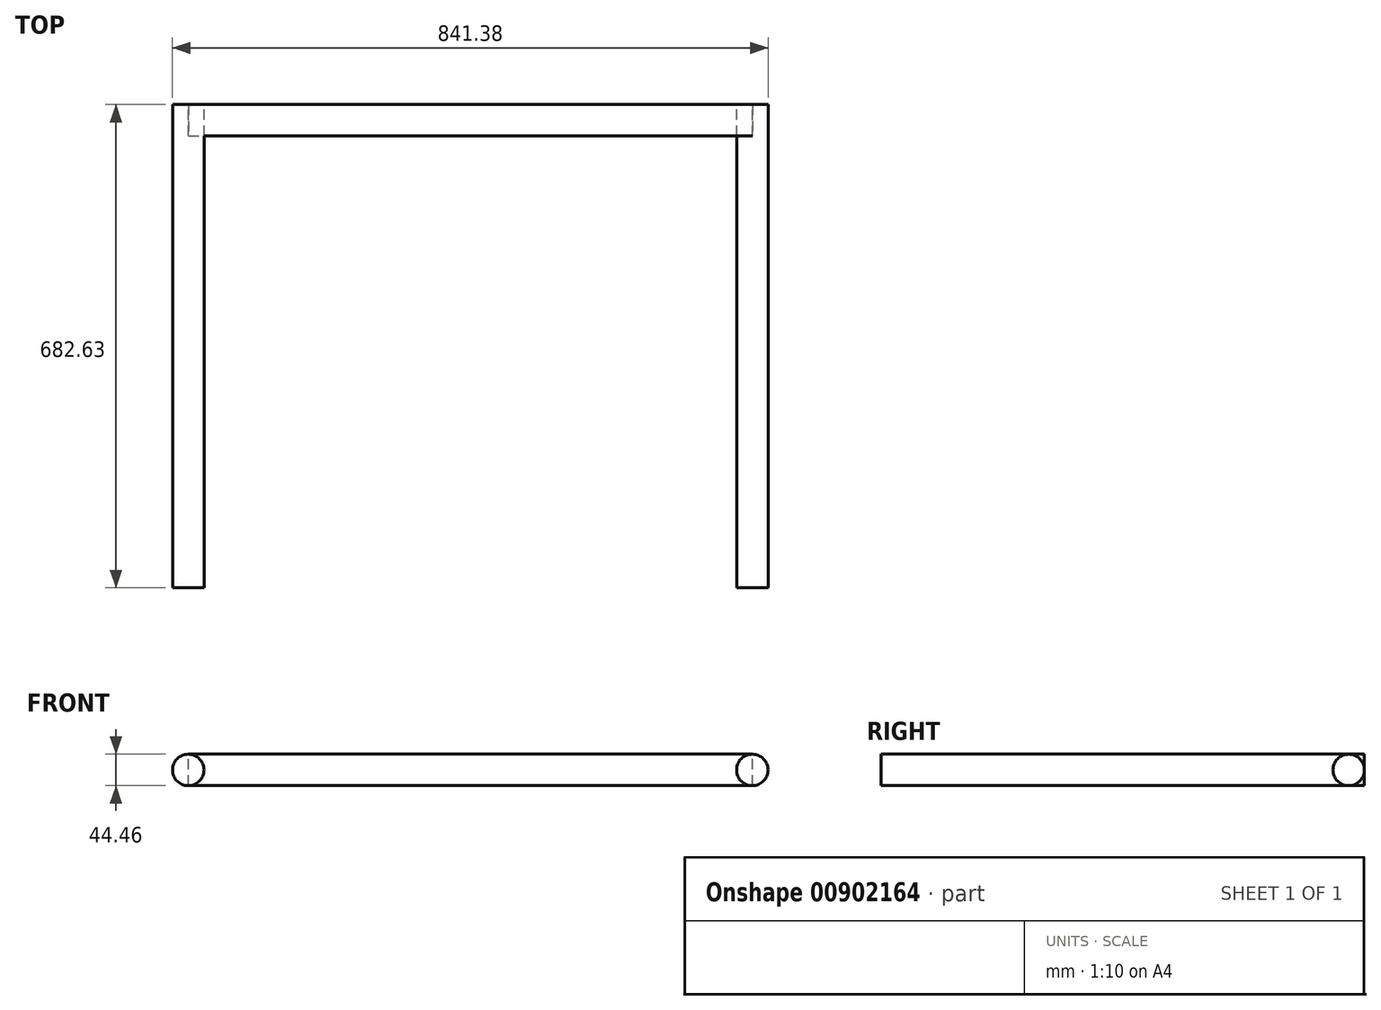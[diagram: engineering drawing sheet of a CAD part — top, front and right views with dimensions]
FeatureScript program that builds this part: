
annotation { "Feature Type Name" : "Feature", "Feature Type Description" : "" }
export const myFeature = defineFeature(function(context is Context, id is Id, definition is map)
    precondition{}
    {
        {
            var Q0;
            Q0=qCreatedBy(makeId("Front.planeOp"),FACE);
            var sketch = newSketch(context, id + "F0", { "sketchPlane" : qUnion([Q0])});
            skLineSegment(sketch, "E0", {"start": v(0, 0) * mm, "end": v(0, -387.35) * mm, "construction": true});
            skLineSegment(sketch, "E1", {"start": v(0, -387.35) * mm, "end": v(-398.46, -387.35) * mm, "construction": true});
            skLineSegment(sketch, "E2", {"start": v(0, -387.35) * mm, "end": v(398.46, -387.35) * mm, "construction": true});
            skSolve(sketch);
        }
        {
            var Q0;
            Q0=qCreatedBy(makeId("Front.planeOp"),FACE);
            var sketch = newSketch(context, id + "F1", { "sketchPlane" : qUnion([Q0])});
            skCircle(sketch, "E3", {"center": v(-398.46, -387.35) * mm, "radius": 22.23 * mm});
            skCircle(sketch, "E4", {"center": v(398.46, -387.35) * mm, "radius": 22.23 * mm});
            skSolve(sketch);
        }
        {
            var Q0;
            Q0=sQuery(id+"F0.wireOp",EDGE,"E0");
            var Q1;
            Q1=sQuery(id+"F0.wireOp",VERTEX,"E0.end");
            cPlane(context, id + "F2", {"entities" : qUnion([Q0, Q1]), "cplaneType" : CPlaneType.LINE_POINT, "offset" : 25.4 * mm, "width" : 152.4 * mm, "height" : 152.4 * mm});
        }
        {
            var Q0;
            Q0=qCreatedBy(id+"F2.planeOp",FACE);
            var sketch = newSketch(context, id + "F3", { "sketchPlane" : qUnion([Q0])});
            skLineSegment(sketch, "E5", {"start": v(-398.46, 0) * mm, "end": v(-398.46, -660.4) * mm});
            skLineSegment(sketch, "E6", {"start": v(398.46, 0) * mm, "end": v(398.46, -660.4) * mm});
            skLineSegment(sketch, "E7", {"start": v(398.46, -660.4) * mm, "end": v(-398.46, -660.4) * mm});
            skLineSegment(sketch, "E8", {"start": v(-398.46, -660.4) * mm, "end": v(-398.46, -682.62) * mm});
            skLineSegment(sketch, "E9", {"start": v(398.46, -660.4) * mm, "end": v(398.46, -682.62) * mm});
            skSolve(sketch);
        }
        {
            var Q0;
            Q0=qCreatedBy(makeId("Right.planeOp"),FACE);
            var sketch = newSketch(context, id + "F4", { "sketchPlane" : qUnion([Q0])});
            skCircle(sketch, "E10", {"center": v(660.4, -387.35) * mm, "radius": 22.23 * mm});
            skSolve(sketch);
        }
        {
            var Q0;
            Q0=makeQuery(id+"F1.imprint","IMPRINT",FACE,{"disambiguationData":[TD([[makeQuery(id+"F1.imprint","IMPRINT",EDGE,{"derivedFrom":sQuery(id+"F1.wireOp",EDGE,"E3")}),1.0]])]});
            var Q1;
            Q1=sQuery(id+"F3.wireOp",EDGE,"E5");
            var Q2;
            Q2=sQuery(id+"F3.wireOp",EDGE,"E8");
            sweep(context, id + "F5", {"profiles" : qUnion([Q0]), "path" : qUnion([Q1, Q2])});
        }
        {
            var Q0;
            Q0=makeQuery(id+"F1.imprint","IMPRINT",FACE,{"disambiguationData":[TD([[makeQuery(id+"F1.imprint","IMPRINT",EDGE,{"derivedFrom":sQuery(id+"F1.wireOp",EDGE,"E4")}),1.0]])]});
            var Q1;
            Q1=sQuery(id+"F3.wireOp",EDGE,"E6");
            var Q2;
            Q2=sQuery(id+"F3.wireOp",EDGE,"E9");
            sweep(context, id + "F6", {"profiles" : qUnion([Q0]), "path" : qUnion([Q1, Q2])});
        }
        {
            var Q0;
            Q0=makeQuery(id+"F4.imprint","IMPRINT",FACE,{"disambiguationData":[TD([[makeQuery(id+"F4.imprint","IMPRINT",EDGE,{"derivedFrom":sQuery(id+"F4.wireOp",EDGE,"E10")}),1.0]])]});
            var Q1;
            Q1=sQuery(id+"F3.wireOp",EDGE,"E7");
            sweep(context, id + "F7", {"profiles" : qUnion([Q0]), "path" : qUnion([Q1])});
        }
    });
